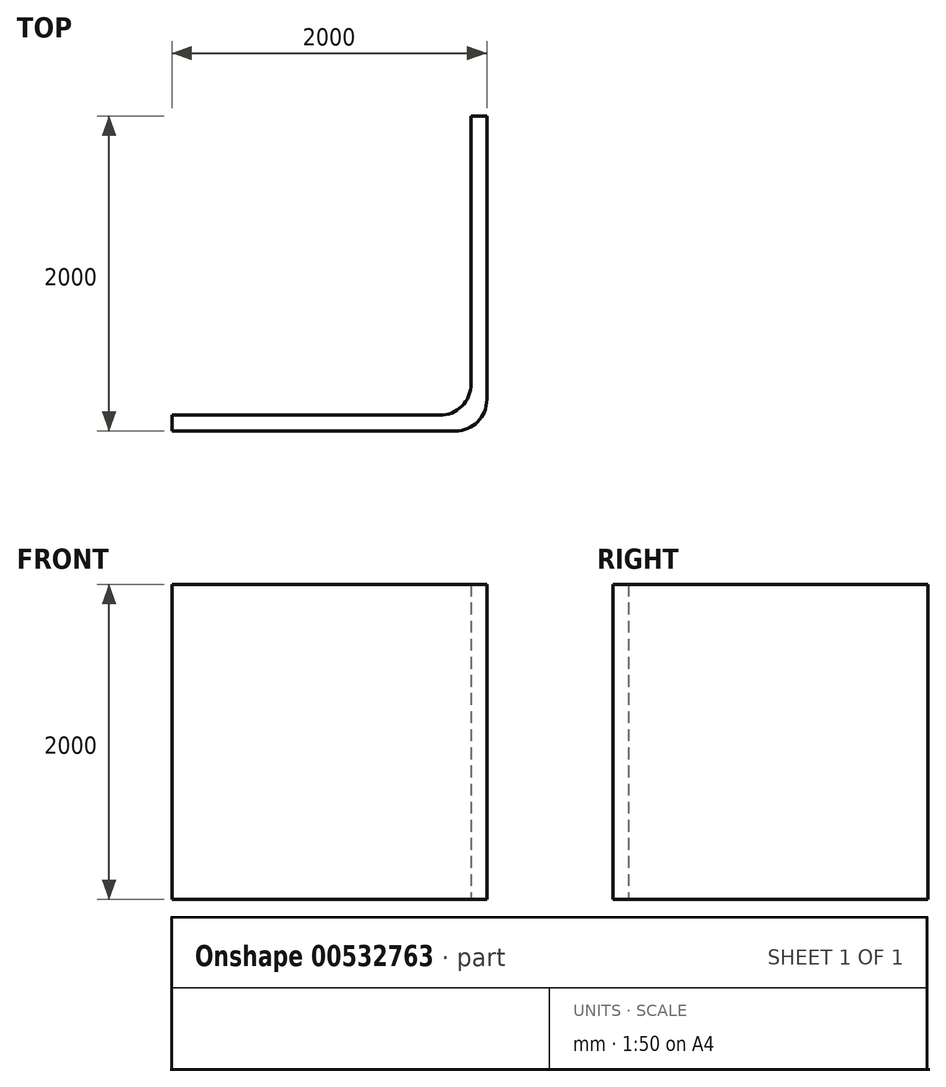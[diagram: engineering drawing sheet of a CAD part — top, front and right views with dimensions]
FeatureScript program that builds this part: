
annotation { "Feature Type Name" : "Feature", "Feature Type Description" : "" }
export const myFeature = defineFeature(function(context is Context, id is Id, definition is map)
    precondition{}
    {
        {
            var Q0;
            Q0=qCreatedBy(makeId("Top.planeOp"),FACE);
            var sketch = newSketch(context, id + "F0", { "sketchPlane" : qUnion([Q0])});
            skLineSegment(sketch, "E0", {"start": v(0, 0) * mm, "end": v(2000, 0) * mm});
            skLineSegment(sketch, "E1", {"start": v(2000, 0) * mm, "end": v(2000, 2000) * mm});
            skLineSegment(sketch, "E2.0", {"start": v(1900, 100) * mm, "end": v(1900, 2000) * mm});
            skLineSegment(sketch, "E2.1", {"start": v(0, 100) * mm, "end": v(1900, 100) * mm});
            skLineSegment(sketch, "E3", {"start": v(0, 100) * mm, "end": v(0, 0) * mm});
            skLineSegment(sketch, "E4", {"start": v(1900, 2000) * mm, "end": v(2000, 2000) * mm});
            skSolve(sketch);
        }
        {
            var Q0;
            Q0=makeQuery(id+"F0.imprint","IMPRINT",FACE,{"disambiguationData":[TD([[makeQuery(id+"F0.imprint","IMPRINT",EDGE,{"derivedFrom":sQuery(id+"F0.wireOp",EDGE,"E0")}),1.0]])]});
            extrude(context, id + "F1", {"entities" : qUnion([Q0]), "depth" : 2000 * mm, "offsetDistance" : 25 * mm});
        }
        {
            var Q0;
            Q0=makeQuery(id+"F1.opExtrude","SWEPT_EDGE",EDGE,{"disambiguationData":[OSD([sQuery(id+"F0.wireOp",EDGE,"E2.0"),sQuery(id+"F0.wireOp",EDGE,"E2.1")])]});
            var Q1;
            Q1=makeQuery(id+"F1.opExtrude","SWEPT_EDGE",EDGE,{"disambiguationData":[OSD([sQuery(id+"F0.wireOp",EDGE,"E0"),sQuery(id+"F0.wireOp",EDGE,"E1")])]});
            fillet(context, id + "F2", {"entities" : qUnion([Q0, Q1]), "radius" : 200 * mm, "tangentPropagation" : true, "allowEdgeOverflow" : false});
        }
    });
